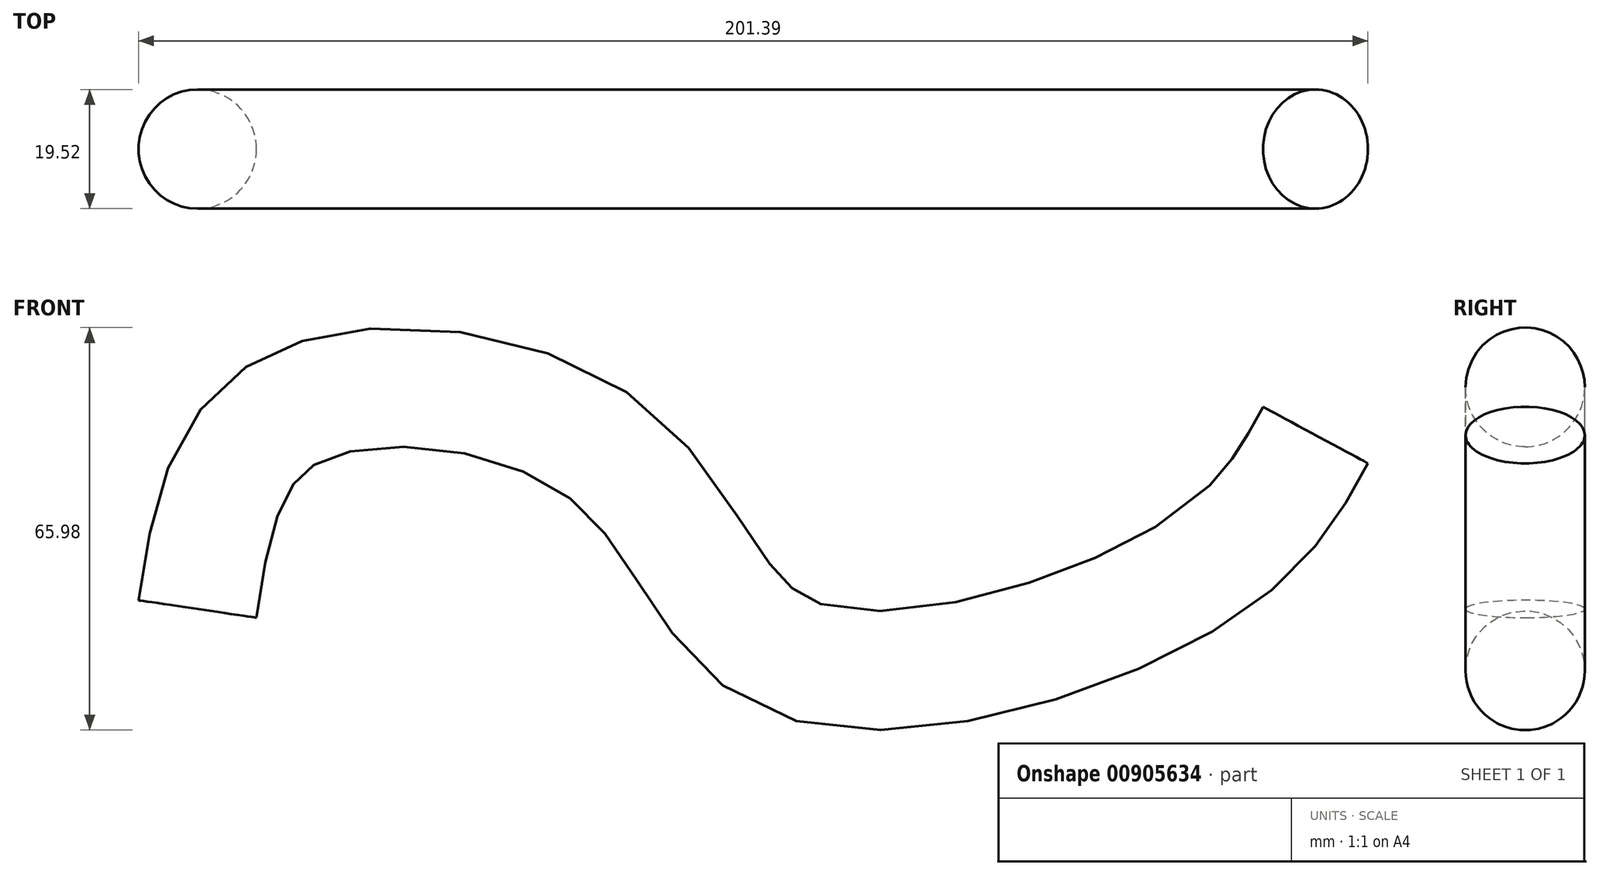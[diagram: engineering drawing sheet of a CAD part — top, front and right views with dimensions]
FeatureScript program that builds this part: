
annotation { "Feature Type Name" : "Feature", "Feature Type Description" : "" }
export const myFeature = defineFeature(function(context is Context, id is Id, definition is map)
    precondition{}
    {
        {
            var Q0;
            Q0=qCreatedBy(makeId("Front.planeOp"),FACE);
            var sketch = newSketch(context, id + "F0", { "sketchPlane" : qUnion([Q0])});
            skFitSpline(sketch, "E0", {"points": [v(-82.59, -21.1) * mm, v(-68.27, 10.98) * mm, v(-15.37, 4.3) * mm, v(14.23, -28.93) * mm, v(81.44, -14.8) * mm, v(100.54, 7.35) * mm], "startDerivative": vector(32.7, 220.93) * mm, "endDerivative": vector(75.15, 139.43) * mm});
            skSolve(sketch);
        }
        {
            var Q0;
            Q0=sQuery(id+"F0.wireOp",EDGE,"E0");
            var Q1;
            Q1=sQuery(id+"F0.wireOp",VERTEX,"E0.end");
            cPlane(context, id + "F1", {"entities" : qUnion([Q0, Q1]), "cplaneType" : CPlaneType.CURVE_POINT, "offset" : 25.4 * mm, "width" : 152.4 * mm, "height" : 152.4 * mm});
        }
        {
            var Q0;
            Q0=qCreatedBy(id+"F1.planeOp",FACE);
            var sketch = newSketch(context, id + "F2", { "sketchPlane" : qUnion([Q0])});
            skCircle(sketch, "E1", {"center": v(84.86, 0) * mm, "radius": 9.76 * mm});
            skSolve(sketch);
        }
        {
            var Q0;
            Q0=makeQuery(id+"F2.imprint","IMPRINT",FACE,{"disambiguationData":[TD([[makeQuery(id+"F2.imprint","IMPRINT",EDGE,{"derivedFrom":sQuery(id+"F2.wireOp",EDGE,"E1")}),1.0]])]});
            var Q1;
            Q1=sQuery(id+"F0.wireOp",EDGE,"E0");
            sweep(context, id + "F3", {"profiles" : qUnion([Q0]), "path" : qUnion([Q1])});
        }
    });
